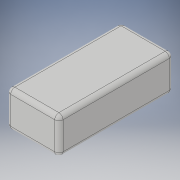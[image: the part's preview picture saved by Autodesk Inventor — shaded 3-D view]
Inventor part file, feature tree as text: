
AUTODESK INVENTOR PART (.ipt)
format: ipt  version: 2018 (Build 220112000, 112)  size: 114,176 bytes
history: native  units: in
note: dims shown in document units (in); Inventor stores cm internally (conversion verified against a paired STEP export)
features: extrude x1, fillet x1, sketch x1
ambient origin geometry x8: Origin, YZ Plane, XZ Plane, XY Plane, X Axis, Y Axis, Z Axis, Center Point
bodies: Solid1 (feature_tree)
feature tree (3):
  extrude  "Extrusion1"  Depth=2.7559in
  fillet  "Fillet1"  Radius=0.8661in
  sketch  "Sketch1"  dims[d0=1.2598in d1=2.7559in d2=0.8661in d3=0.0in d4=0.1in]
